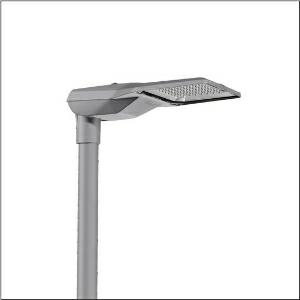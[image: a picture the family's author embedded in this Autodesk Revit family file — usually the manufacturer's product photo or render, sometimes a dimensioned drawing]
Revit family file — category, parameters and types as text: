
# Revit family: streetlight_sl_21_midi___pl52_5xe3h33s08mb_0b8e
name_source: partatom
category: Lighting Fixtures
units: mm (PartAtom-declared; Revit-internal decimal feet)

## family parameters
Cut with Voids When Loaded = No
Host = Face
Light Source = No
Part Type = Normal
Room Calculation Point = No
Round Connector Dimension = Use Diameter
Shared = No

## types (1)
- --- (1 x LED, 17960 lm, 136 W, 3000K)
    Apparent Load = 136 VA
    CIE Flux Codes = 27 59 98 100 100
    Color Rendering = 70
    Color Temperature = 3000K
    Default Elevation = 1800 mm
    Description = Streetlight SL 21 midi, mast luminaire, primary light control with lens, of PMMA, primary optical cover: cover, of toughened safety glass, transparent, light distribution: PL52, light emission: direct distribution, primary light characteristic: asymmetric, installation type: side-entry, post-top, LED, High Power LED, rated luminous flux: 17.960lm, luminous efficacy: 132lm/W, light colour: 730, colour temperature: 3000K, control gear: D4i, control: overheat protection, constant luminous flux control, time-dependent luminous flux control, flexible luminous flux parameterisation, pre-setting: logarithmic dimming characteristic, mains connection: 230..240V, AC, 50/60Hz, start of lifetime: 136W, end of service life: 142W, reduction: 61W, luminaire housing, of diecast aluminium, powder-coated, Siteco® metallic grey (DB 702S), corrosivity category C5 mid according to DIN EN ISO 12944, please order mast flange separately, inclination adjustable: 0°, 5°, 10°, 15°, sealing non-destructively replaceable, multi-level sealing system, length: 644mm, width: 335mm, height: 110mm, mast flange for spigot size: 42mm (side-entry): 5XC10008XM4, 60/48mm (side-entry/post-top): 5XC10108XM2, 76/60mm (side-entry/post-top): 5XC10108XM1, mounting height: 4..8m, Smart Interface above, protection rating (complete): IP66, insulation class (complete): insulation class II (safety insulation), certification: CE, ENEC, ENEC+, VDE, impact resistance: IK10, permissible operating ambient temperature for outdoor applications: -40..+50°C, standard-compliant lighting for roads and squares, packaging unit: 1 piece

Light Distribution: PL52
    Height = 111 mm
    Lamp = 1 x LED
    Lamp Light Flux = 17960 lm
    Lamp Power = 136 W
    Lamp count = 1
    Length = 644 mm
    Luminous efficacy = 132 lm/W
    Manufacturer = Siteco
    ModVariant = No
    Model = 5XE3H33S08MB
    Number of Poles = 1
    OnlyDefault = Yes
    Power Factor = 1
    Product Name = Streetlight SL 21 midi | PL52
    Product group = mast luminaire | pylon top
    ProductGroupID = 6100
    Protection Class = Protection class II
    Protection Degree = IP 66
    RLX_Detail_Level = 1
    RLX_Emergency_Light_Flux = 0 lm
    RLX_Emergency_Type = 0
    RLX_Emergency_Type_DB = No
    RlxData = <blob elided: 36493 chars, md5=489bb56f>
    Socket = socket
    Standby Power = 0 W
    System Light Flux = 17960 lm
    System Power = 136 W
    Type Comments = factory setting: luminous flux: 100 % | dim-lin: 254 | 695 mA
    Type Image = l_1004302.jpg
    URL = http://relux.com
    VarID = @adj_190664
    Voltage = 0 V
    Weight = 0.00 kg
    Width = 336 mm

## geometry (parser evidence)
native form markers: Blend x4, Sweep x10
no freeform markers — native parametric forms only
